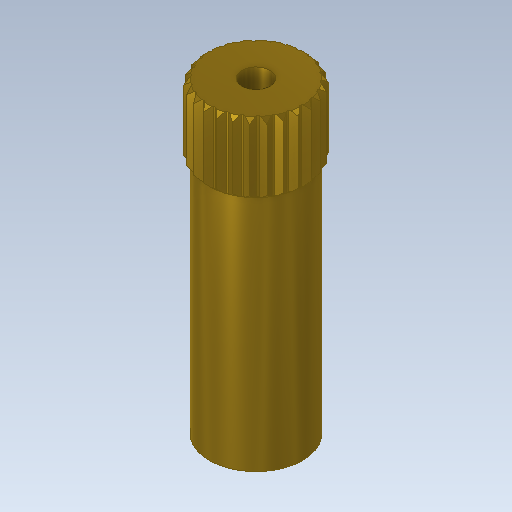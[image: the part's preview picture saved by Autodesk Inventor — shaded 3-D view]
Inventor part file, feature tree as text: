
AUTODESK INVENTOR PART (.ipt)
format: ipt  version: 2020 (Build 240168000, 168)  size: 365,568 bytes
history: native  units: mm
features: extrude x6, sketch x6, pattern_circular x2, plane x2, projected_geometry x2, other x1, mirror x1
ambient origin geometry x8: Origin, YZ Plane, XZ Plane, XY Plane, X Axis, Y Axis, Z Axis, Center Point
bodies: Body1 (feature_tree)
feature tree (20):
  other  "Sólido1"
  extrude  "Extrusión1"  Depth=13.5mm TaperAngle=0.0deg
  extrude  "Extrusión2"  Depth=4.0mm TaperAngle=0.0deg
  extrude  "Extrusión3"  Depth=4.0mm TaperAngle=360.0deg
  pattern_circular  "Patrón circular1"  Angle=45.0deg  [1 undecoded]
  plane  "Plano de trabajo1"
  extrude  "Extrusión4"  Depth=13.5mm
  pattern_circular  "Patrón circular2"  [2 undecoded]
  extrude  "Extrusión5"  Depth=13.5mm TaperAngle=360.0deg
  extrude  "Extrusión6"  Depth=13.5mm
  plane  "Plano de trabajo3"
  mirror  "Simetría2"
  sketch  "Boceto1"  dims[d0=5.8mm d1=13.5mm d2=0.0mm]
  sketch  "Boceto2"  dims[d3=0.3mm d4=4.0mm d5=0.0mm]
  projected_geometry  "Contorno proyectado1"
  sketch  "Boceto3"  dims[d9=4.0mm d10=0.0mm d11=260.0mm d12=360.0deg]
  projected_geometry  "Contorno proyectado2"
  sketch  "Boceto5"  dims[d21=0.3mm]
  sketch  "Boceto6"  dims[d22=13.962634mm]
  sketch  "Boceto7"  dims[d23=8.726646mm d25=45.0deg d26=0.25mm d27=0.7mm d28=0.0mm d29=260.0mm d30=360.0deg d32=1.6mm d33=4.0mm d34=0.0mm d36=13.5mm d37=0.0mm d38=5.3mm]
note: 3 required parameter values undecoded (feature->parameter linkage not recoverable at this tier; creation-order binding heuristic only, values carry confidence <= 0.55)
